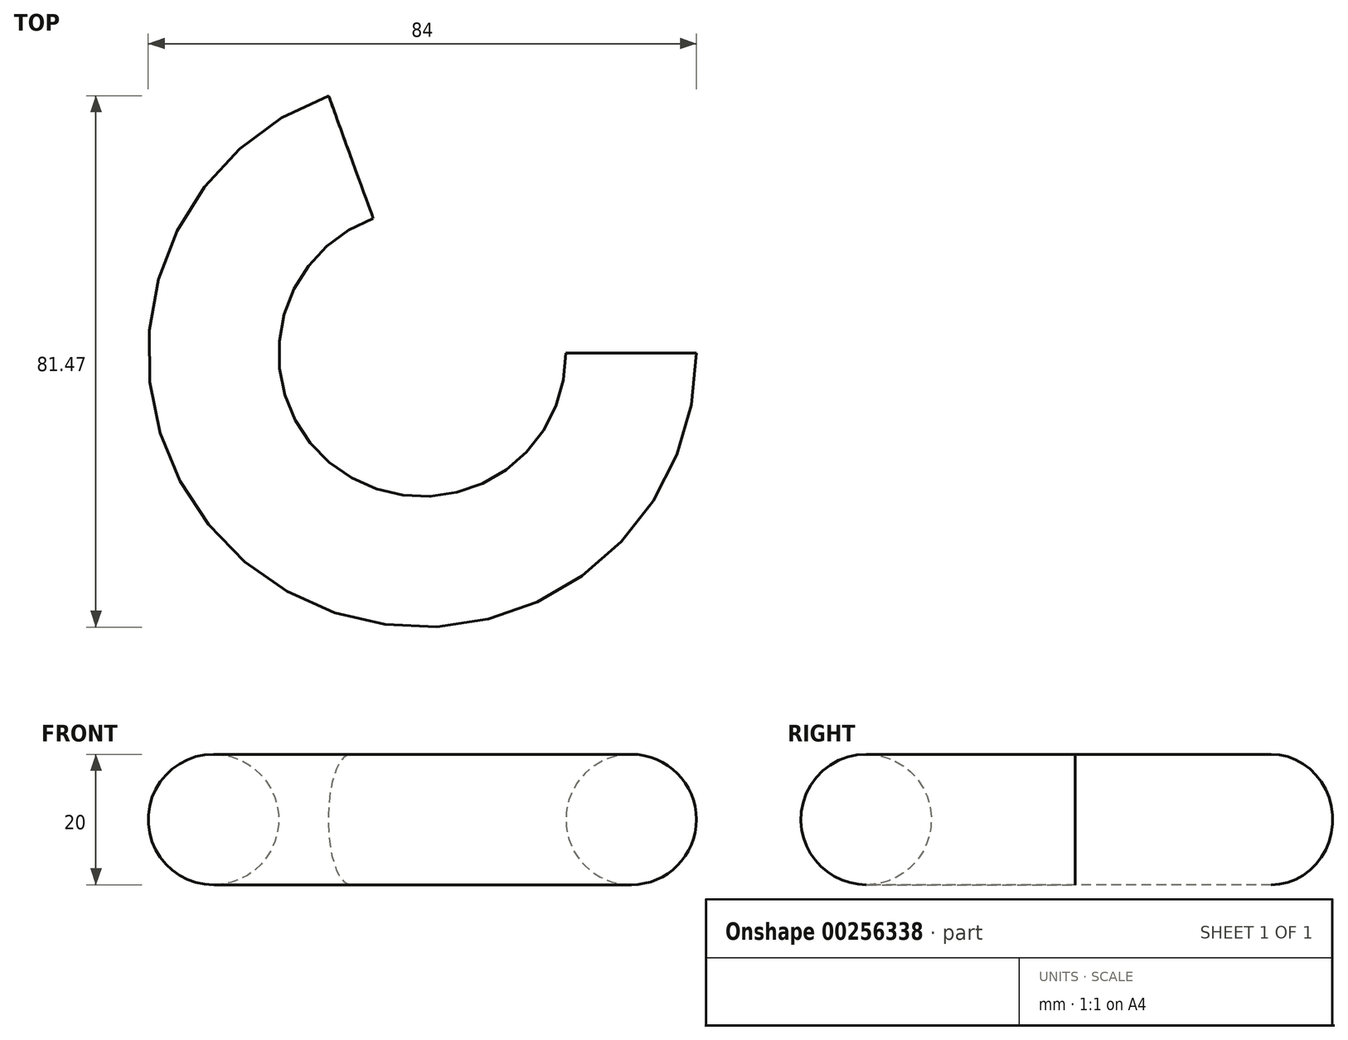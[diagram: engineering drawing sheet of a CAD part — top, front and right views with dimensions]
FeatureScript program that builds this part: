
annotation { "Feature Type Name" : "Feature", "Feature Type Description" : "" }
export const myFeature = defineFeature(function(context is Context, id is Id, definition is map)
    precondition{}
    {
        {
            var Q0;
            Q0=qCreatedBy(makeId("Front.planeOp"),FACE);
            var sketch = newSketch(context, id + "F0", { "sketchPlane" : qUnion([Q0])});
            skCircle(sketch, "E0", {"center": v(32, 0) * mm, "radius": 10 * mm});
            skLineSegment(sketch, "E1", {"start": v(0, 42.9) * mm, "end": v(0, -62.02) * mm, "construction": true});
            skSolve(sketch);
        }
        {
            var Q0;
            Q0=makeQuery(id+"F0.imprint","IMPRINT",FACE,{"disambiguationData":[TD([[makeQuery(id+"F0.imprint","IMPRINT",EDGE,{"derivedFrom":sQuery(id+"F0.wireOp",EDGE,"E0")}),1.0]])]});
            var Q1;
            Q1=sQuery(id+"F0.wireOp",EDGE,"E1");
            revolve(context, id + "F1", {"entities" : qUnion([Q0]), "axis" : qUnion([Q1]), "revolveType" : RevolveType.ONE_DIRECTION, "angle" : 250 * degree});
        }
    });
